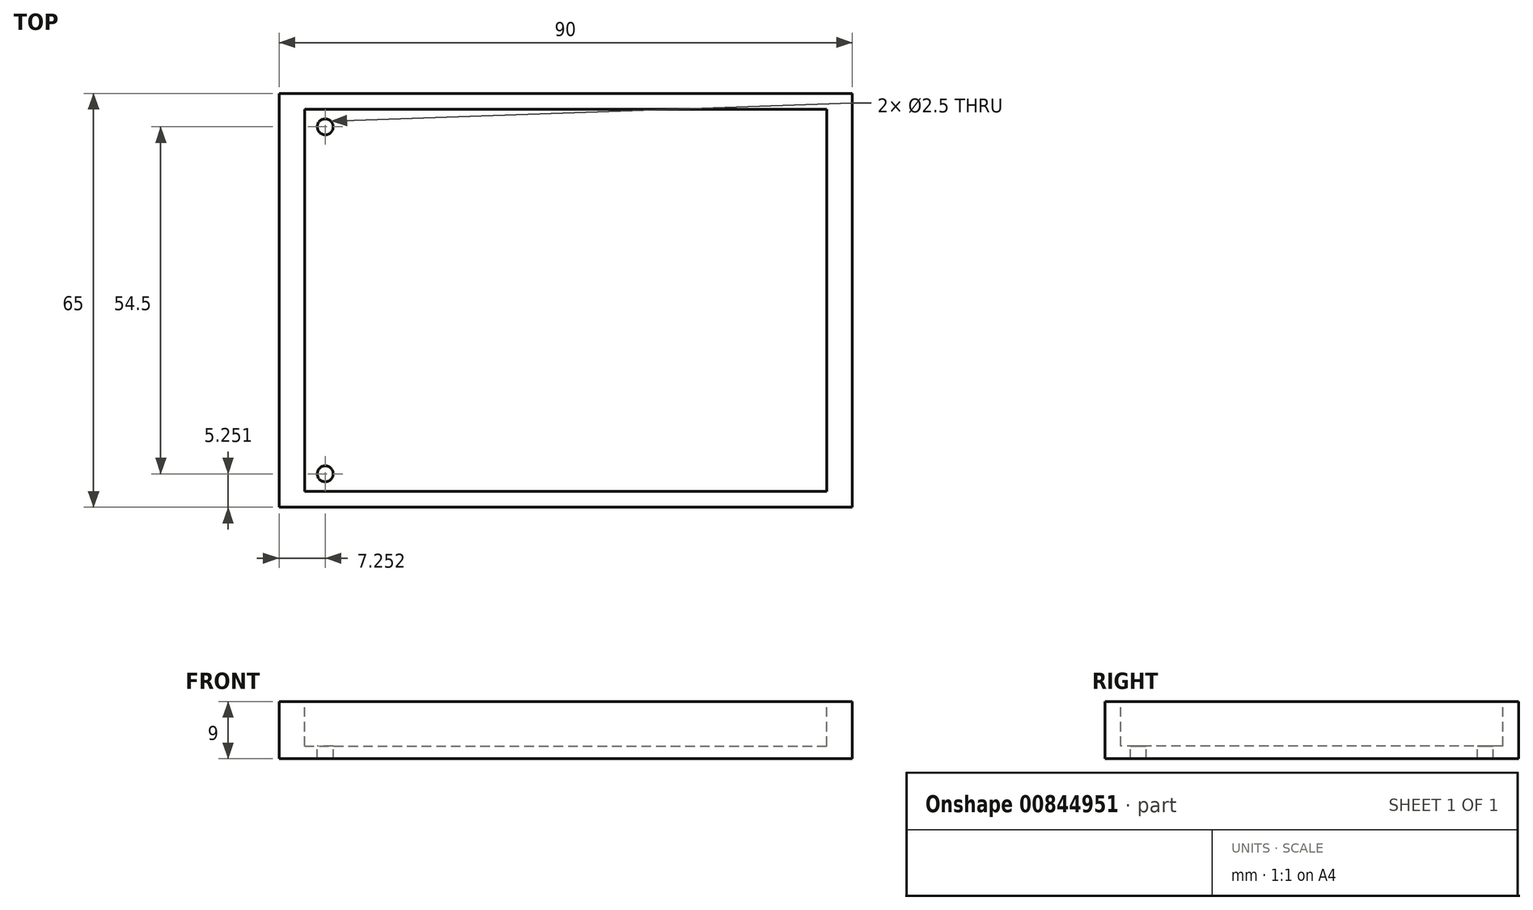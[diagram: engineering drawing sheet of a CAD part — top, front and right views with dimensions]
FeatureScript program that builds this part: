
annotation { "Feature Type Name" : "Feature", "Feature Type Description" : "" }
export const myFeature = defineFeature(function(context is Context, id is Id, definition is map)
    precondition{}
    {
        {
            var Q0;
            Q0=qCreatedBy(makeId("Top.planeOp"),FACE);
            var sketch = newSketch(context, id + "F0", { "sketchPlane" : qUnion([Q0])});
            skLineSegment(sketch, "E0.bottom", {"start": v(-35.9, 35.65) * mm, "end": v(54.1, 35.65) * mm});
            skLineSegment(sketch, "E0.top", {"start": v(-35.9, -29.35) * mm, "end": v(54.1, -29.35) * mm});
            skLineSegment(sketch, "E0.left", {"start": v(-35.9, 35.65) * mm, "end": v(-35.9, -29.35) * mm});
            skLineSegment(sketch, "E0.right", {"start": v(54.1, 35.65) * mm, "end": v(54.1, -29.35) * mm});
            skSolve(sketch);
        }
        {
            var Q0;
            Q0 = qSketchRegion(id + "F0", true);
            extrude(context, id + "F1", {"entities" : qUnion([Q0]), "depth" : 9 * mm, "offsetDistance" : 25 * mm});
        }
        {
            var Q0;
            Q0=makeQuery(id+"F1.opExtrude","CAP_FACE",FACE,{"disambiguationData":[OSD([sQuery(id+"F0.wireOp",EDGE,"E0.bottom"),sQuery(id+"F0.wireOp",EDGE,"E0.top"),sQuery(id+"F0.wireOp",EDGE,"E0.left"),sQuery(id+"F0.wireOp",EDGE,"E0.right")])],"isStart":false});
            var sketch = newSketch(context, id + "F2", { "sketchPlane" : qUnion([Q0])});
            skLineSegment(sketch, "E1.bottom", {"start": v(-31.9, 33.15) * mm, "end": v(50.1, 33.15) * mm});
            skLineSegment(sketch, "E1.top", {"start": v(-31.9, -26.85) * mm, "end": v(50.1, -26.85) * mm});
            skLineSegment(sketch, "E1.left", {"start": v(-31.9, 33.15) * mm, "end": v(-31.9, -26.85) * mm});
            skLineSegment(sketch, "E1.right", {"start": v(50.1, 33.15) * mm, "end": v(50.1, -26.85) * mm});
            skSolve(sketch);
        }
        {
            var Q0;
            Q0 = qSketchRegion(id + "F2", true);
            extrude(context, id + "F3", {"entities" : qUnion([Q0]), "operationType" : NewBodyOperationType.REMOVE, "oppositeDirection" : true, "depth" : 7 * mm, "offsetDistance" : 25 * mm});
        }
        {
            var Q0;
            Q0=makeQuery(id+"F3.boolean.opBoolean","COPY",FACE,{"derivedFrom":makeQuery(id+"F3.opExtrude","CAP_FACE",FACE,{"disambiguationData":[OSD([sQuery(id+"F2.wireOp",EDGE,"E1.bottom"),sQuery(id+"F2.wireOp",EDGE,"E1.top"),sQuery(id+"F2.wireOp",EDGE,"E1.left"),sQuery(id+"F2.wireOp",EDGE,"E1.right")])],"isStart":false})});
            var sketch = newSketch(context, id + "F4", { "sketchPlane" : qUnion([Q0])});
            skCircle(sketch, "E2", {"center": v(-28.66, 30.4) * mm, "radius": 1.25 * mm});
            skCircle(sketch, "E3", {"center": v(-28.66, -24.1) * mm, "radius": 1.25 * mm});
            skSolve(sketch);
        }
        {
            var Q0;
            Q0 = qSketchRegion(id + "F4", true);
            extrude(context, id + "F5", {"entities" : qUnion([Q0]), "operationType" : NewBodyOperationType.REMOVE, "endBound" : BoundingType.THROUGH_ALL, "oppositeDirection" : true, "depth" : 25 * mm, "offsetDistance" : 25 * mm});
        }
    });
